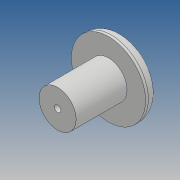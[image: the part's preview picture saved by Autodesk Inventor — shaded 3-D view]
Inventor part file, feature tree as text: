
AUTODESK INVENTOR PART (.ipt)
format: ipt  version: 2017 (Build 210142000, 142)  size: 110,592 bytes
history: native  units: mm
features: revolve x1, sketch x1
ambient origin geometry x8: Origin, YZ Plane, XZ Plane, XY Plane, X Axis, Y Axis, Z Axis, Center Point
bodies: Solid1 (feature_tree)
feature tree (2):
  revolve  "Revolution1"  [1 undecoded]
  sketch  "Sketch1"  dims[d0=4.0mm d1=0.7mm d2=7.0mm d3=1.5mm d4=8.0mm d5=0.3mm d6=90.0deg]
note: 1 required parameter value undecoded (feature->parameter linkage not recoverable at this tier; creation-order binding heuristic only, values carry confidence <= 0.55)
